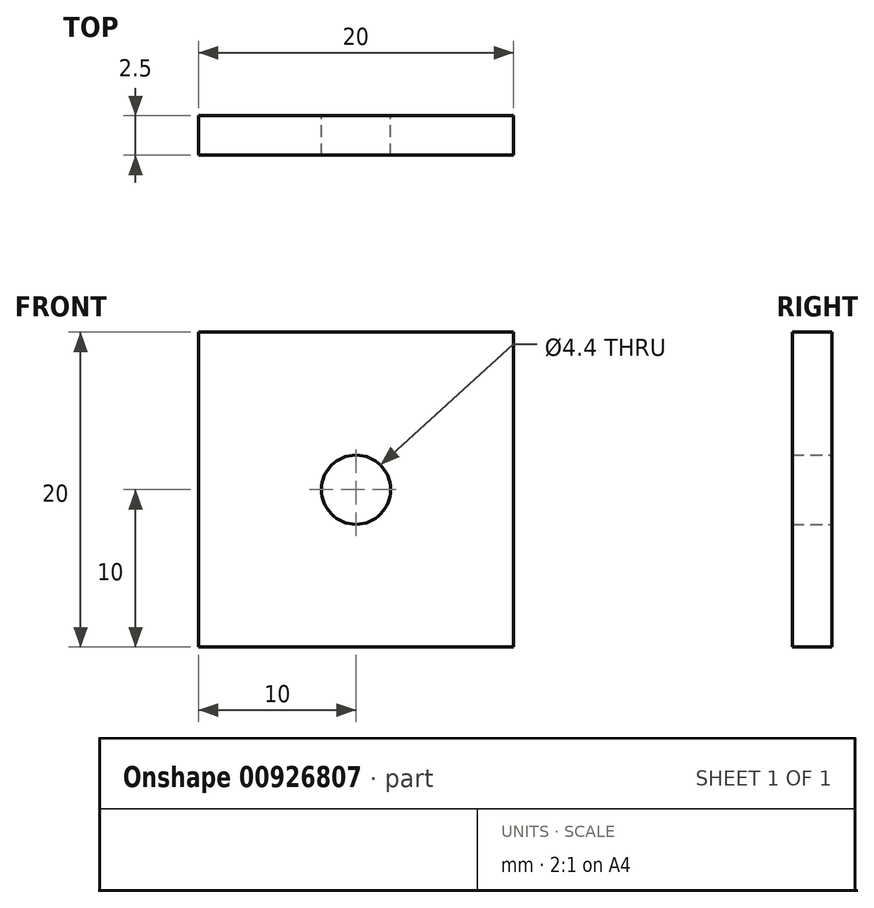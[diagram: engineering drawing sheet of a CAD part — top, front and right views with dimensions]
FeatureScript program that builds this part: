
annotation { "Feature Type Name" : "Feature", "Feature Type Description" : "" }
export const myFeature = defineFeature(function(context is Context, id is Id, definition is map)
    precondition{}
    {
        {
            var Q0;
            Q0=qCreatedBy(makeId("Front.planeOp"),FACE);
            var sketch = newSketch(context, id + "F0", { "sketchPlane" : qUnion([Q0])});
            skLineSegment(sketch, "E0.bottom", {"start": v(-10, -10) * mm, "end": v(10, -10) * mm});
            skLineSegment(sketch, "E0.top", {"start": v(-10, 10) * mm, "end": v(10, 10) * mm});
            skLineSegment(sketch, "E0.left", {"start": v(-10, -10) * mm, "end": v(-10, 10) * mm});
            skLineSegment(sketch, "E0.right", {"start": v(10, -10) * mm, "end": v(10, 10) * mm});
            skPoint(sketch, "E0.middle", {"position": v(0, 0) * mm});
            skSolve(sketch);
        }
        {
            var Q0;
            Q0=qCreatedBy(makeId("Front.planeOp"),FACE);
            var sketch = newSketch(context, id + "F1", { "sketchPlane" : qUnion([Q0])});
            skCircle(sketch, "E1", {"center": v(0, 0) * mm, "radius": 2.2 * mm});
            skSolve(sketch);
        }
        {
            var Q0;
            Q0=makeQuery(id+"F0.imprint","IMPRINT",FACE,{"disambiguationData":[TD([[makeQuery(id+"F0.imprint","IMPRINT",EDGE,{"derivedFrom":sQuery(id+"F0.wireOp",EDGE,"E0.bottom")}),1.0]])]});
            extrude(context, id + "F2", {"entities" : qUnion([Q0]), "depth" : 2.5 * mm, "offsetDistance" : 25 * mm});
        }
        {
            var Q0;
            Q0=makeQuery(id+"F1.imprint","IMPRINT",FACE,{"disambiguationData":[TD([[makeQuery(id+"F1.imprint","IMPRINT",EDGE,{"derivedFrom":sQuery(id+"F1.wireOp",EDGE,"E1")}),1.0]])]});
            extrude(context, id + "F3", {"entities" : qUnion([Q0]), "operationType" : NewBodyOperationType.REMOVE, "depth" : 50 * mm, "offsetDistance" : 25 * mm});
        }
    });
